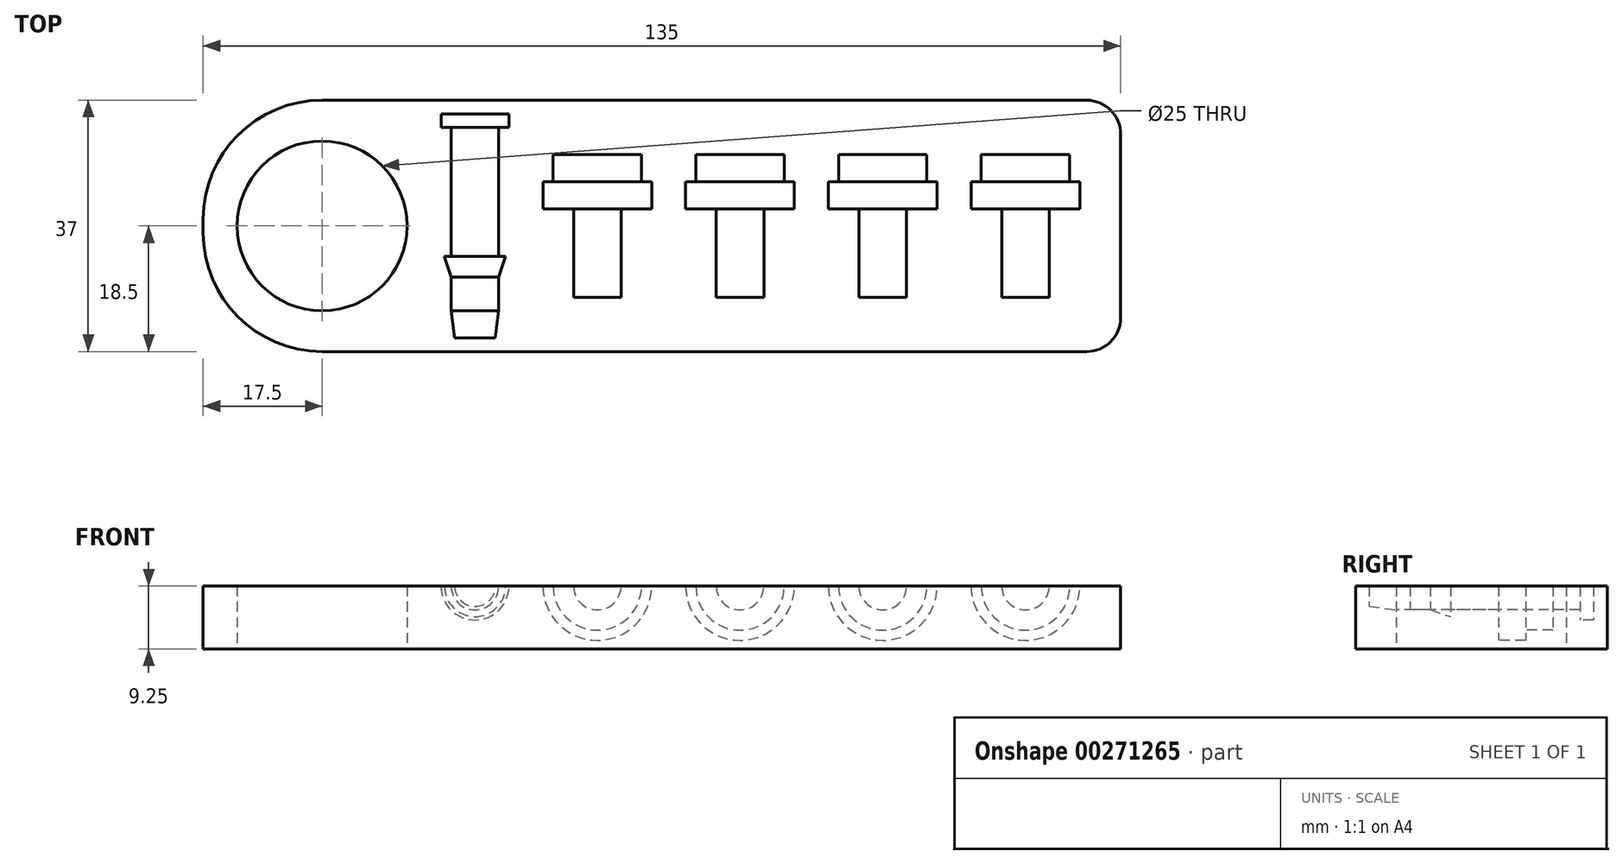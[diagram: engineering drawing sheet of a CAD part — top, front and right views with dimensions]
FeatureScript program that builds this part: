
annotation { "Feature Type Name" : "Feature", "Feature Type Description" : "" }
export const myFeature = defineFeature(function(context is Context, id is Id, definition is map)
    precondition{}
    {
        {
            var Q0;
            Q0=qCreatedBy(makeId("Top.planeOp"),FACE);
            var sketch = newSketch(context, id + "F0", { "sketchPlane" : qUnion([Q0])});
            skLineSegment(sketch, "E0.bottom", {"start": v(17.5, 0) * mm, "end": v(130, 0) * mm});
            skLineSegment(sketch, "E0.top", {"start": v(17.5, 37) * mm, "end": v(130, 37) * mm});
            skLineSegment(sketch, "E0.left", {"start": v(0, 17.5) * mm, "end": v(0, 19.5) * mm});
            skLineSegment(sketch, "E0.right", {"start": v(135, 5) * mm, "end": v(135, 32) * mm});
            skLineSegment(sketch, "E1.bottom", {"start": v(0, 0) * mm, "end": v(17.5, 0) * mm, "construction": true});
            skLineSegment(sketch, "E1.top", {"start": v(0, 18.5) * mm, "end": v(17.5, 18.5) * mm, "construction": true});
            skLineSegment(sketch, "E1.left", {"start": v(0, 0) * mm, "end": v(0, 18.5) * mm, "construction": true});
            skLineSegment(sketch, "E1.right", {"start": v(17.5, 0) * mm, "end": v(17.5, 18.5) * mm, "construction": true});
            skCircle(sketch, "E2", {"center": v(17.5, 18.5) * mm, "radius": 12.5 * mm});
            skPoint(sketch, "E3.visualSharp", {"position": v(0, 0) * mm});
            skArc(sketch, "E3.filletArc", {"start": v(0, 17.5) * mm, "mid": v(5.13, 5.13) * mm, "end": v(17.5, 0) * mm});
            skPoint(sketch, "E4.visualSharp", {"position": v(0, 37) * mm});
            skArc(sketch, "E4.filletArc", {"start": v(17.5, 37) * mm, "mid": v(5.13, 31.87) * mm, "end": v(0, 19.5) * mm});
            skPoint(sketch, "E5.visualSharp", {"position": v(135, 37) * mm});
            skArc(sketch, "E5.filletArc", {"start": v(135, 32) * mm, "mid": v(133.54, 35.54) * mm, "end": v(130, 37) * mm});
            skPoint(sketch, "E6.visualSharp", {"position": v(135, 0) * mm});
            skArc(sketch, "E6.filletArc", {"start": v(130, 0) * mm, "mid": v(133.54, 1.46) * mm, "end": v(135, 5) * mm});
            skSolve(sketch);
        }
        {
            var Q0;
            Q0=makeQuery(id+"F0.imprint","IMPRINT",FACE,{"disambiguationData":[TD([[makeQuery(id+"F0.imprint","IMPRINT",EDGE,{"derivedFrom":sQuery(id+"F0.wireOp",EDGE,"E0.bottom")}),1.0]])]});
            extrude(context, id + "F1", {"entities" : qUnion([Q0]), "depth" : 9.25 * mm});
        }
        {
            var Q0;
            Q0=makeQuery(id+"F1.opExtrude","CAP_FACE",FACE,{"disambiguationData":[OSD([sQuery(id+"F0.wireOp",EDGE,"E0.bottom"),sQuery(id+"F0.wireOp",EDGE,"E0.top"),sQuery(id+"F0.wireOp",EDGE,"E0.right"),sQuery(id+"F0.wireOp",EDGE,"E2"),sQuery(id+"F0.wireOp",EDGE,"E3.filletArc"),sQuery(id+"F0.wireOp",EDGE,"E4.filletArc"),sQuery(id+"F0.wireOp",EDGE,"E5.filletArc"),sQuery(id+"F0.wireOp",EDGE,"E6.filletArc")])],"isStart":false});
            var sketch = newSketch(context, id + "F2", { "sketchPlane" : qUnion([Q0])});
            skLineSegment(sketch, "E7.bottom", {"start": v(0, 0) * mm, "end": v(40, 0) * mm, "construction": true});
            skLineSegment(sketch, "E7.top", {"start": v(0, 35) * mm, "end": v(40, 35) * mm, "construction": true});
            skLineSegment(sketch, "E7.left", {"start": v(0, 0) * mm, "end": v(0, 35) * mm, "construction": true});
            skLineSegment(sketch, "E8.bottom", {"start": v(40, 35) * mm, "end": v(58, 35) * mm, "construction": true});
            skLineSegment(sketch, "E8.left", {"start": v(40, 35) * mm, "end": v(40, 29) * mm, "construction": true});
            skLineSegment(sketch, "E8.right", {"start": v(58, 35) * mm, "end": v(58, 29) * mm, "construction": true});
            skLineSegment(sketch, "E9", {"start": v(58, 29) * mm, "end": v(79, 29) * mm, "construction": true});
            skLineSegment(sketch, "E10", {"start": v(79, 29) * mm, "end": v(100, 29) * mm, "construction": true});
            skLineSegment(sketch, "E11", {"start": v(100, 29) * mm, "end": v(121, 29) * mm, "construction": true});
            skLineSegment(sketch, "E12.bottom", {"start": v(40, 35) * mm, "end": v(45, 35) * mm});
            skLineSegment(sketch, "E12.top", {"start": v(43.5, 33) * mm, "end": v(45, 33) * mm});
            skLineSegment(sketch, "E12.left", {"start": v(40, 35) * mm, "end": v(40, 33) * mm});
            skLineSegment(sketch, "E12.right", {"start": v(45, 35) * mm, "end": v(45, 33) * mm});
            skLineSegment(sketch, "E13.left", {"start": v(40, 33) * mm, "end": v(40, 13) * mm});
            skLineSegment(sketch, "E13.right", {"start": v(43.5, 33) * mm, "end": v(43.5, 14) * mm});
            skLineSegment(sketch, "E14", {"start": v(43.5, 14) * mm, "end": v(44.5, 14) * mm});
            skLineSegment(sketch, "E15", {"start": v(43.5, 11) * mm, "end": v(43.5, 6) * mm});
            skLineSegment(sketch, "E16", {"start": v(43, 2) * mm, "end": v(40, 2) * mm});
            skLineSegment(sketch, "E17", {"start": v(40, 2) * mm, "end": v(40, 13) * mm});
            skLineSegment(sketch, "E18", {"start": v(44.5, 14) * mm, "end": v(43.5, 11) * mm});
            skLineSegment(sketch, "E19.bottom", {"start": v(58, 29) * mm, "end": v(64.5, 29) * mm});
            skLineSegment(sketch, "E19.left", {"start": v(58, 29) * mm, "end": v(58, 25) * mm});
            skLineSegment(sketch, "E19.right", {"start": v(64.5, 29) * mm, "end": v(64.5, 25) * mm});
            skLineSegment(sketch, "E20.bottom", {"start": v(64.5, 25) * mm, "end": v(66, 25) * mm});
            skLineSegment(sketch, "E20.top", {"start": v(61.5, 21) * mm, "end": v(66, 21) * mm});
            skLineSegment(sketch, "E20.left", {"start": v(58, 25) * mm, "end": v(58, 21) * mm});
            skLineSegment(sketch, "E20.right", {"start": v(66, 25) * mm, "end": v(66, 21) * mm});
            skLineSegment(sketch, "E21.top", {"start": v(58, 8) * mm, "end": v(61.5, 8) * mm});
            skLineSegment(sketch, "E21.left", {"start": v(58, 21) * mm, "end": v(58, 8) * mm});
            skLineSegment(sketch, "E21.right", {"start": v(61.5, 21) * mm, "end": v(61.5, 8) * mm});
            skLineSegment(sketch, "E22.bottom", {"start": v(79, 29) * mm, "end": v(85.5, 29) * mm});
            skLineSegment(sketch, "E22.left", {"start": v(79, 29) * mm, "end": v(79, 25) * mm});
            skLineSegment(sketch, "E22.right", {"start": v(85.5, 29) * mm, "end": v(85.5, 25) * mm});
            skLineSegment(sketch, "E23.bottom", {"start": v(100, 29) * mm, "end": v(106.5, 29) * mm});
            skLineSegment(sketch, "E23.left", {"start": v(100, 29) * mm, "end": v(100, 25) * mm});
            skLineSegment(sketch, "E23.right", {"start": v(106.5, 29) * mm, "end": v(106.5, 25) * mm});
            skLineSegment(sketch, "E24.bottom", {"start": v(121, 29) * mm, "end": v(127.5, 29) * mm});
            skLineSegment(sketch, "E24.left", {"start": v(121, 29) * mm, "end": v(121, 25) * mm});
            skLineSegment(sketch, "E24.right", {"start": v(127.5, 29) * mm, "end": v(127.5, 25) * mm});
            skLineSegment(sketch, "E25.bottom", {"start": v(85.5, 25) * mm, "end": v(87, 25) * mm});
            skLineSegment(sketch, "E25.top", {"start": v(82.5, 21) * mm, "end": v(87, 21) * mm});
            skLineSegment(sketch, "E25.left", {"start": v(79, 25) * mm, "end": v(79, 21) * mm});
            skLineSegment(sketch, "E25.right", {"start": v(87, 25) * mm, "end": v(87, 21) * mm});
            skLineSegment(sketch, "E26.bottom", {"start": v(106.5, 25) * mm, "end": v(108, 25) * mm});
            skLineSegment(sketch, "E26.top", {"start": v(103.5, 21) * mm, "end": v(108, 21) * mm});
            skLineSegment(sketch, "E26.left", {"start": v(100, 25) * mm, "end": v(100, 21) * mm});
            skLineSegment(sketch, "E26.right", {"start": v(108, 25) * mm, "end": v(108, 21) * mm});
            skLineSegment(sketch, "E27.bottom", {"start": v(127.5, 25) * mm, "end": v(129, 25) * mm});
            skLineSegment(sketch, "E27.top", {"start": v(124.5, 21) * mm, "end": v(129, 21) * mm});
            skLineSegment(sketch, "E27.left", {"start": v(121, 25) * mm, "end": v(121, 21) * mm});
            skLineSegment(sketch, "E27.right", {"start": v(129, 25) * mm, "end": v(129, 21) * mm});
            skLineSegment(sketch, "E28.top", {"start": v(79, 8) * mm, "end": v(82.5, 8) * mm});
            skLineSegment(sketch, "E28.left", {"start": v(79, 21) * mm, "end": v(79, 8) * mm});
            skLineSegment(sketch, "E28.right", {"start": v(82.5, 21) * mm, "end": v(82.5, 8) * mm});
            skLineSegment(sketch, "E29.top", {"start": v(100, 8) * mm, "end": v(103.5, 8) * mm});
            skLineSegment(sketch, "E29.left", {"start": v(100, 21) * mm, "end": v(100, 8) * mm});
            skLineSegment(sketch, "E29.right", {"start": v(103.5, 21) * mm, "end": v(103.5, 8) * mm});
            skLineSegment(sketch, "E30.top", {"start": v(121, 8) * mm, "end": v(124.5, 8) * mm});
            skLineSegment(sketch, "E30.left", {"start": v(121, 21) * mm, "end": v(121, 8) * mm});
            skLineSegment(sketch, "E30.right", {"start": v(124.5, 21) * mm, "end": v(124.5, 8) * mm});
            skLineSegment(sketch, "E31", {"start": v(43.5, 6) * mm, "end": v(43, 2) * mm});
            skSolve(sketch);
        }
        {
            var Q0;
            Q0=makeQuery(id+"F2.imprint","IMPRINT",FACE,{"disambiguationData":[TD([[makeQuery(id+"F2.imprint","IMPRINT",EDGE,{"derivedFrom":sQuery(id+"F2.wireOp",EDGE,"E12.bottom")}),-1.0]])]});
            var Q1;
            Q1=sQuery(id+"F2.wireOp",EDGE,"E13.left");
            revolve(context, id + "F3", {"operationType" : NewBodyOperationType.REMOVE, "entities" : qUnion([Q0]), "axis" : qUnion([Q1]), "revolveType" : RevolveType.FULL, "oppositeDirection" : true});
        }
        {
            var Q0;
            Q0=makeQuery(id+"F2.imprint","IMPRINT",FACE,{"disambiguationData":[TD([[makeQuery(id+"F2.imprint","IMPRINT",EDGE,{"derivedFrom":sQuery(id+"F2.wireOp",EDGE,"E19.bottom")}),-1.0]])]});
            var Q1;
            Q1=sQuery(id+"F2.wireOp",EDGE,"E21.left");
            revolve(context, id + "F4", {"operationType" : NewBodyOperationType.REMOVE, "entities" : qUnion([Q0]), "axis" : qUnion([Q1]), "revolveType" : RevolveType.FULL, "oppositeDirection" : true});
        }
        {
            var Q0;
            Q0=makeQuery(id+"F2.imprint","IMPRINT",FACE,{"disambiguationData":[TD([[makeQuery(id+"F2.imprint","IMPRINT",EDGE,{"derivedFrom":sQuery(id+"F2.wireOp",EDGE,"E22.bottom")}),-1.0]])]});
            var Q1;
            Q1=sQuery(id+"F2.wireOp",EDGE,"E28.left");
            revolve(context, id + "F5", {"operationType" : NewBodyOperationType.REMOVE, "entities" : qUnion([Q0]), "axis" : qUnion([Q1]), "revolveType" : RevolveType.FULL, "oppositeDirection" : true});
        }
        {
            var Q0;
            Q0=makeQuery(id+"F2.imprint","IMPRINT",FACE,{"disambiguationData":[TD([[makeQuery(id+"F2.imprint","IMPRINT",EDGE,{"derivedFrom":sQuery(id+"F2.wireOp",EDGE,"E23.bottom")}),-1.0]])]});
            var Q1;
            Q1=sQuery(id+"F2.wireOp",EDGE,"E29.left");
            revolve(context, id + "F6", {"operationType" : NewBodyOperationType.REMOVE, "entities" : qUnion([Q0]), "axis" : qUnion([Q1]), "revolveType" : RevolveType.FULL, "oppositeDirection" : true});
        }
        {
            var Q0;
            Q0=makeQuery(id+"F2.imprint","IMPRINT",FACE,{"disambiguationData":[TD([[makeQuery(id+"F2.imprint","IMPRINT",EDGE,{"derivedFrom":sQuery(id+"F2.wireOp",EDGE,"E24.bottom")}),-1.0]])]});
            var Q1;
            Q1=sQuery(id+"F2.wireOp",EDGE,"E30.left");
            revolve(context, id + "F7", {"operationType" : NewBodyOperationType.REMOVE, "entities" : qUnion([Q0]), "axis" : qUnion([Q1]), "revolveType" : RevolveType.FULL, "oppositeDirection" : true});
        }
    });
